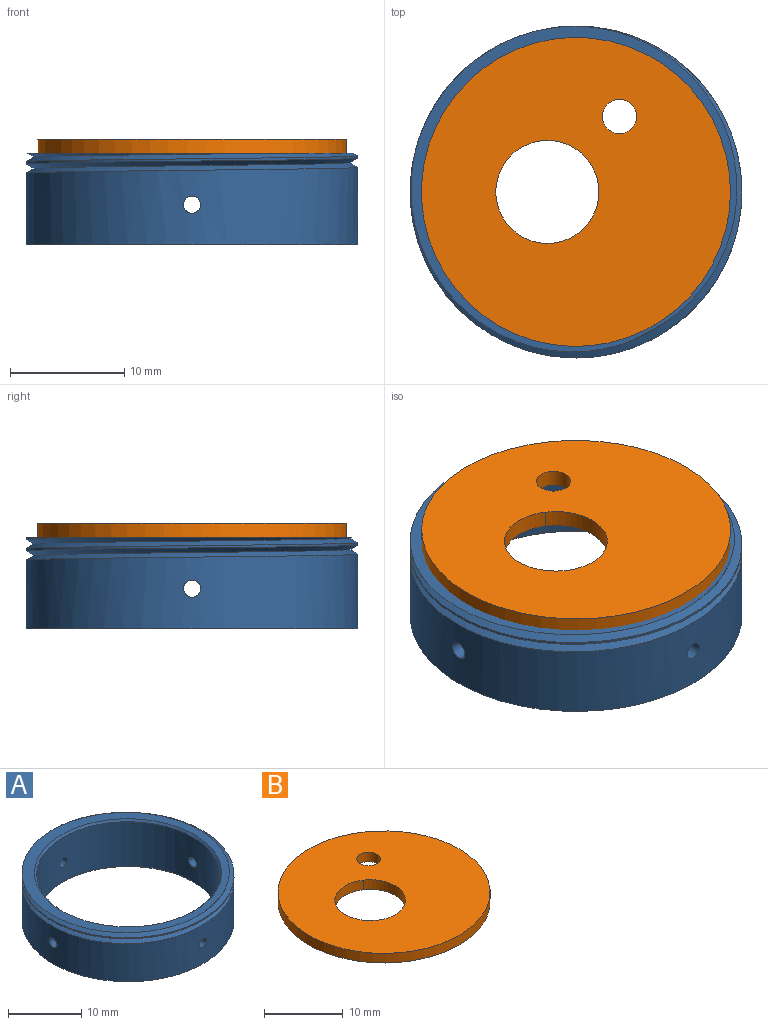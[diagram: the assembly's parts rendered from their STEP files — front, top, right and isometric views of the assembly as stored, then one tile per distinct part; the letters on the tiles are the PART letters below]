
ASSEMBLY  parts=2 mates=1
PART A: 15 faces, bbox 29.5x34x9.1 mm
  f0: cylinder r=14.5mm len=29mm, axis (0,0,-1), area 562.3mm2, adj f1,f5,f6,f7,f11,f12,f13,f14
  f1: cylinder r=14.5mm len=29mm, axis (0,0,-1), area 18.2mm2, adj f0,f2,f7,f8
  f2: cylinder r=14.5mm len=28.25mm, axis (0,0,-1), area 6.4mm2, adj f1,f4,f7,f8
  f3: cylinder r=12.5mm len=25mm, axis (0,0,-1), area 574.1mm2, adj f9,f10,f11,f12,f13,f14
  f4: plane 29.02x29.02mm, normal (0,0,1), area 121mm2, adj f2,f7,f8,f9
  f5: plane 29x29mm, normal (0,0,-1), area 145.8mm2, adj f0,f10
  f6: plane 0.8x0.69mm, normal (0,1,0), area 0.3mm2, adj f0,f7,f8
  f7: bspline ~33.49x29mm, area 146mm2, adj f0,f1,f2,f4,f6,f8
  f8: bspline ~33.49x29mm, area 117.3mm2, adj f1,f2,f4,f6,f7
  f9: cone r=12.5mm half-angle=45deg, axis (0,0,1), area 33.7mm2, adj f3,f4
  f10: cone r=12.8mm half-angle=45deg, axis (0,0,-1), area 33.7mm2, adj f3,f5
  f11: cylinder r=0.75mm len=2mm, axis (0,-1,0), area 9.4mm2, adj f0,f3
  f12: cylinder r=0.75mm len=2mm, axis (0,-1,0), area 9.4mm2, adj f0,f3
  f13: cylinder r=0.75mm len=2mm, axis (1,0,0), area 9.4mm2, adj f0,f3
  f14: cylinder r=0.75mm len=2mm, axis (1,0,0), area 9.4mm2, adj f0,f3
PART B: 10 faces, bbox 27x27x1.5 mm
  f0: cylinder r=3.75mm len=1.5mm, axis (0,0,-1), area 0mm2, adj f1,f6,f7,f8
  f1: cylinder r=4.5mm len=9mm, axis (0,0,-1), area 29.1mm2, adj f0,f2,f7,f8
  f2: cylinder r=3.75mm len=1.5mm, axis (0,0,-1), area 0mm2, adj f1,f3,f7,f8
  f3: plane 1.5x0.01mm, normal (-1,0,0), area 0mm2, adj f2,f4,f7,f8
  f4: cylinder r=4.5mm len=7.48mm, axis (0,0,-1), area 13.3mm2, adj f3,f6,f7,f8
  f5: cylinder r=13.5mm len=27mm, axis (0,0,-1), area 127.2mm2, adj f7,f8
  f6: plane 1.5x0.01mm, normal (-1,0,0), area 0mm2, adj f0,f4,f7,f8
  f7: plane 27x27mm, normal (0,0,1), area 501.9mm2, adj f0,f1,f2,f3,f4,f5,f6,f9
  f8: plane 27x27mm, normal (0,0,-1), area 501.9mm2, adj f0,f1,f2,f3,f4,f5,f6,f9
  f9: cylinder r=1.5mm len=3mm, axis (0,0,-1), area 14.1mm2, adj f7,f8
PLACE A t=(57.75,-0.67,-9.82)mm
PLACE B t=(56.48,-1.52,-2.12)mm
MATE fastened A.f3 <-> B.f0  axis (0,0,1) through (57.75,-0.67,-2.12)mm
